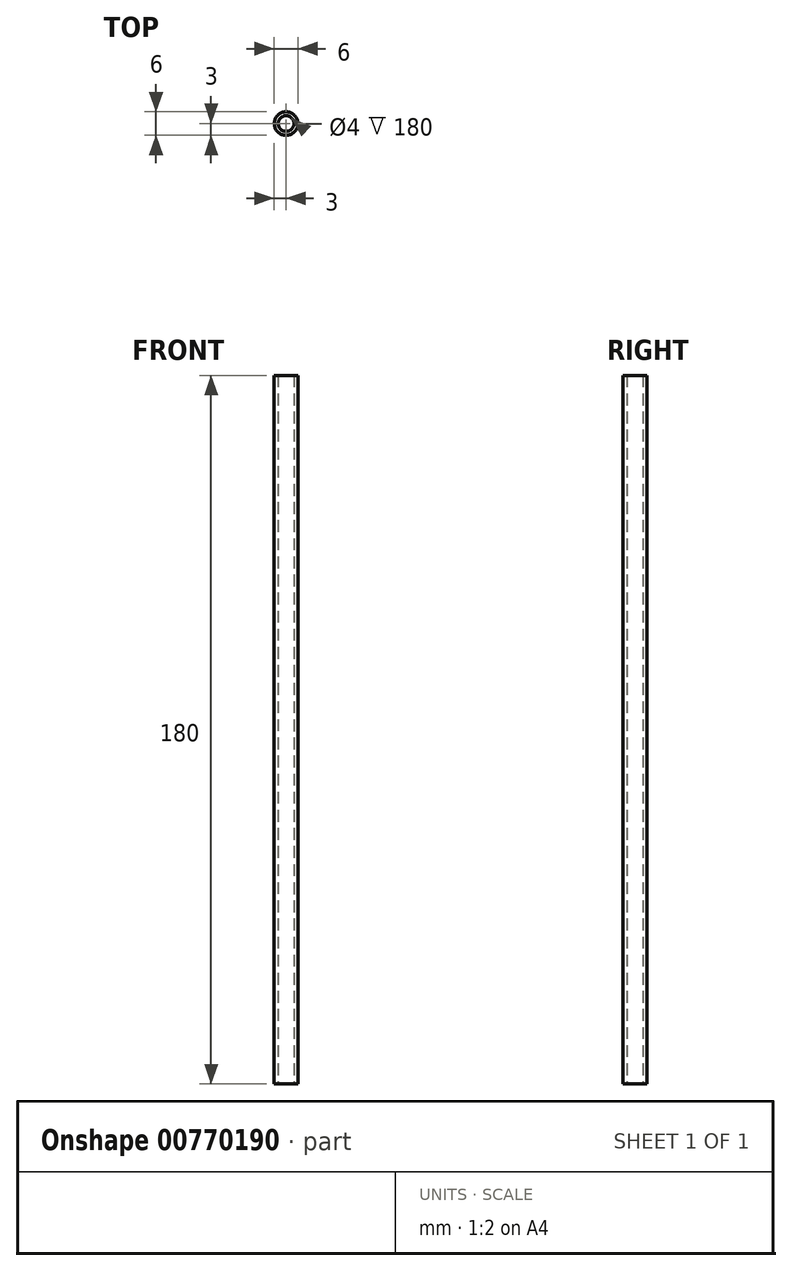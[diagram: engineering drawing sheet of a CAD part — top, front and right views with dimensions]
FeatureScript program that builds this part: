
annotation { "Feature Type Name" : "Feature", "Feature Type Description" : "" }
export const myFeature = defineFeature(function(context is Context, id is Id, definition is map)
    precondition{}
    {
        {
            var Q0;
            Q0=qCreatedBy(makeId("Top.planeOp"),FACE);
            var sketch = newSketch(context, id + "F0", { "sketchPlane" : qUnion([Q0])});
            skCircle(sketch, "E0", {"center": v(0, 0) * mm, "radius": 2 * mm});
            skCircle(sketch, "E1", {"center": v(0, 0) * mm, "radius": 3 * mm});
            skSolve(sketch);
        }
        {
            var Q0;
            Q0=makeQuery(id+"F0.imprint","IMPRINT",FACE,{"disambiguationData":[TD([[makeQuery(id+"F0.imprint","IMPRINT",EDGE,{"derivedFrom":sQuery(id+"F0.wireOp",EDGE,"E0")}),-1.0]])]});
            extrude(context, id + "F1", {"entities" : qUnion([Q0]), "depth" : 180 * mm, "offsetDistance" : 25 * mm});
        }
    });
